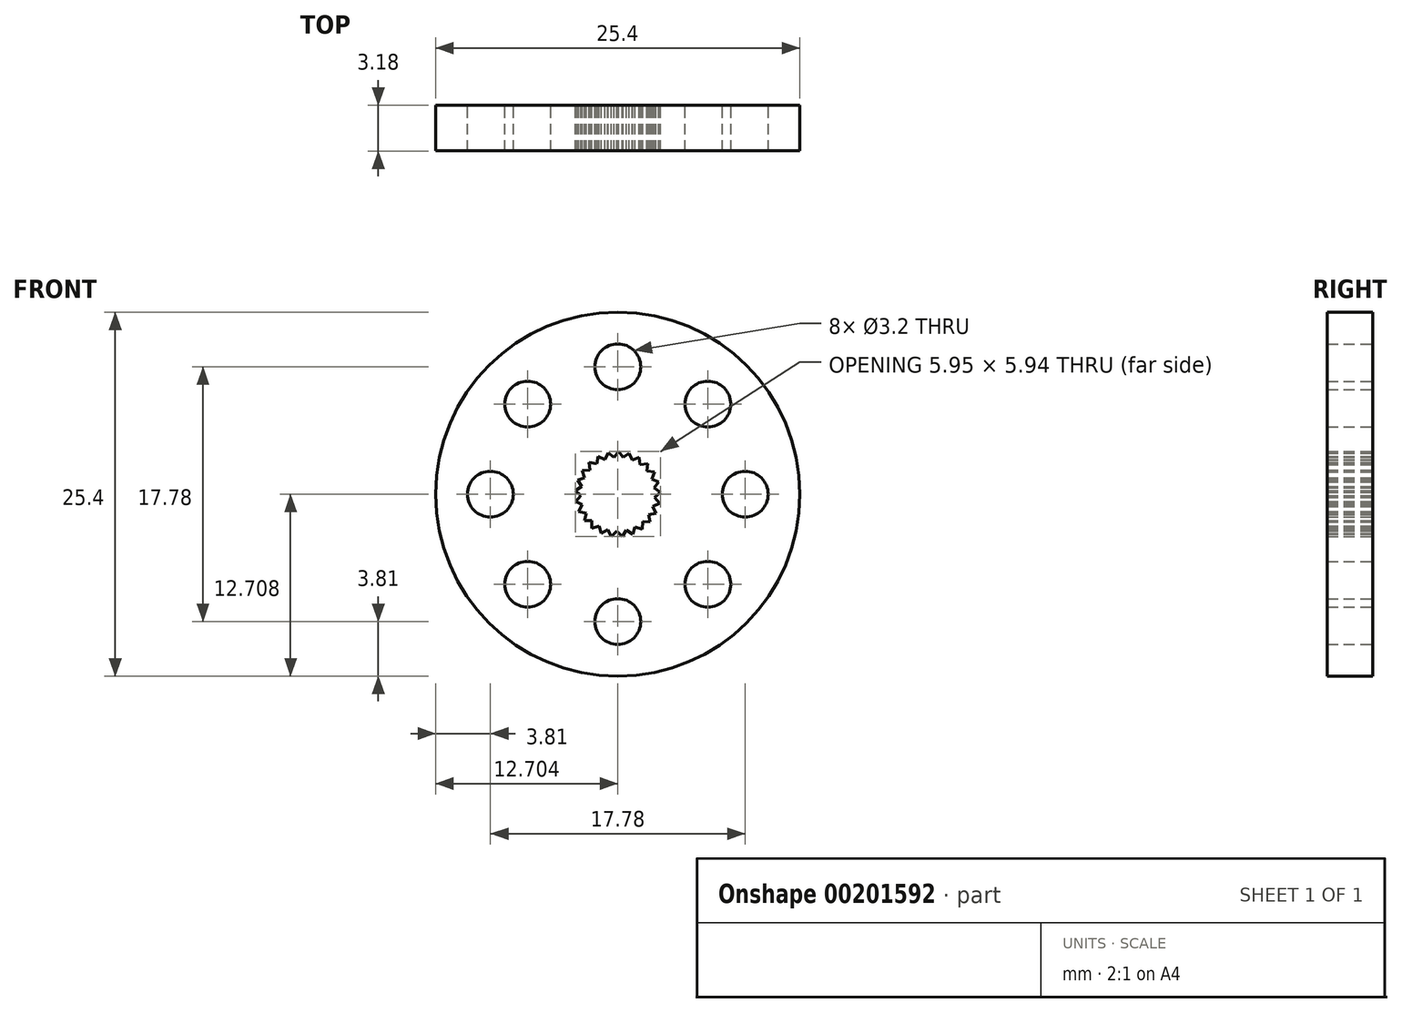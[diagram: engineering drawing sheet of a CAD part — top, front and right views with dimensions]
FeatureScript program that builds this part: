
annotation { "Feature Type Name" : "Feature", "Feature Type Description" : "" }
export const myFeature = defineFeature(function(context is Context, id is Id, definition is map)
    precondition{}
    {
        {
            var Q0;
            Q0=qCreatedBy(makeId("Front.planeOp"),FACE);
            var sketch = newSketch(context, id + "F0", { "sketchPlane" : qUnion([Q0])});
            skCircle(sketch, "E0", {"center": v(0, 0) * mm, "radius": 12.7 * mm});
            skCircle(sketch, "E1", {"center": v(0, 8.9) * mm, "radius": 1.6 * mm});
            skLineSegment(sketch, "E2", {"start": v(-2.48, 1.65) * mm, "end": v(-2.31, 1.15) * mm});
            skLineSegment(sketch, "E3", {"start": v(-2.31, 1.15) * mm, "end": v(-2.81, 0.98) * mm});
            skLineSegment(sketch, "E4.1.0", {"start": v(-2.81, 0.98) * mm, "end": v(-2.53, 0.54) * mm});
            skLineSegment(sketch, "E4.1.1", {"start": v(-2.53, 0.54) * mm, "end": v(-2.97, 0.25) * mm});
            skLineSegment(sketch, "E4.2.0", {"start": v(-2.97, 0.25) * mm, "end": v(-2.58, -0.1) * mm});
            skLineSegment(sketch, "E4.2.1", {"start": v(-2.58, -0.1) * mm, "end": v(-2.94, -0.5) * mm});
            skLineSegment(sketch, "E4.3.0", {"start": v(-2.94, -0.5) * mm, "end": v(-2.47, -0.74) * mm});
            skLineSegment(sketch, "E4.3.1", {"start": v(-2.47, -0.74) * mm, "end": v(-2.72, -1.2) * mm});
            skLineSegment(sketch, "E4.4.0", {"start": v(-2.72, -1.2) * mm, "end": v(-2.21, -1.34) * mm});
            skLineSegment(sketch, "E4.4.1", {"start": v(-2.21, -1.34) * mm, "end": v(-2.34, -1.85) * mm});
            skLineSegment(sketch, "E4.5.0", {"start": v(-2.34, -1.85) * mm, "end": v(-1.8, -1.84) * mm});
            skLineSegment(sketch, "E4.5.1", {"start": v(-1.8, -1.84) * mm, "end": v(-1.8, -2.37) * mm});
            skLineSegment(sketch, "E4.6.0", {"start": v(-1.8, -2.37) * mm, "end": v(-1.3, -2.24) * mm});
            skLineSegment(sketch, "E4.6.1", {"start": v(-1.3, -2.24) * mm, "end": v(-1.16, -2.75) * mm});
            skLineSegment(sketch, "E4.7.0", {"start": v(-1.16, -2.75) * mm, "end": v(-0.7, -2.49) * mm});
            skLineSegment(sketch, "E4.7.1", {"start": v(-0.7, -2.49) * mm, "end": v(-0.44, -2.95) * mm});
            skLineSegment(sketch, "E4.8.0", {"start": v(-0.44, -2.95) * mm, "end": v(-0.06, -2.58) * mm});
            skLineSegment(sketch, "E4.8.1", {"start": v(-0.06, -2.58) * mm, "end": v(0.3, -2.96) * mm});
            skLineSegment(sketch, "E4.9.0", {"start": v(0.3, -2.96) * mm, "end": v(0.59, -2.52) * mm});
            skLineSegment(sketch, "E4.9.1", {"start": v(0.59, -2.52) * mm, "end": v(1.04, -2.8) * mm});
            skLineSegment(sketch, "E4.10.0", {"start": v(1.04, -2.8) * mm, "end": v(1.2, -2.3) * mm});
            skLineSegment(sketch, "E4.10.1", {"start": v(1.2, -2.3) * mm, "end": v(1.7, -2.45) * mm});
            skLineSegment(sketch, "E4.11.0", {"start": v(1.7, -2.45) * mm, "end": v(1.73, -1.92) * mm});
            skLineSegment(sketch, "E4.11.1", {"start": v(1.73, -1.92) * mm, "end": v(2.25, -1.95) * mm});
            skLineSegment(sketch, "E4.12.0", {"start": v(2.25, -1.95) * mm, "end": v(2.15, -1.43) * mm});
            skLineSegment(sketch, "E4.12.1", {"start": v(2.15, -1.43) * mm, "end": v(2.67, -1.33) * mm});
            skLineSegment(sketch, "E4.13.0", {"start": v(2.67, -1.33) * mm, "end": v(2.44, -0.85) * mm});
            skLineSegment(sketch, "E4.13.1", {"start": v(2.44, -0.85) * mm, "end": v(2.91, -0.62) * mm});
            skLineSegment(sketch, "E4.14.0", {"start": v(2.91, -0.62) * mm, "end": v(2.57, -0.22) * mm});
            skLineSegment(sketch, "E4.14.1", {"start": v(2.57, -0.22) * mm, "end": v(2.98, 0.12) * mm});
            skLineSegment(sketch, "E4.15.0", {"start": v(2.98, 0.12) * mm, "end": v(2.55, 0.43) * mm});
            skLineSegment(sketch, "E4.15.1", {"start": v(2.55, 0.43) * mm, "end": v(2.85, 0.86) * mm});
            skLineSegment(sketch, "E4.16.0", {"start": v(2.85, 0.86) * mm, "end": v(2.36, 1.05) * mm});
            skLineSegment(sketch, "E4.16.1", {"start": v(2.36, 1.05) * mm, "end": v(2.55, 1.54) * mm});
            skLineSegment(sketch, "E4.17.0", {"start": v(2.55, 1.54) * mm, "end": v(2.03, 1.6) * mm});
            skLineSegment(sketch, "E4.17.1", {"start": v(2.03, 1.6) * mm, "end": v(2.09, 2.13) * mm});
            skLineSegment(sketch, "E4.18.0", {"start": v(2.09, 2.13) * mm, "end": v(1.56, 2.06) * mm});
            skLineSegment(sketch, "E4.18.1", {"start": v(1.56, 2.06) * mm, "end": v(1.5, 2.58) * mm});
            skLineSegment(sketch, "E4.19.0", {"start": v(1.5, 2.58) * mm, "end": v(1, 2.38) * mm});
            skLineSegment(sketch, "E4.19.1", {"start": v(1, 2.38) * mm, "end": v(0.8, 2.87) * mm});
            skLineSegment(sketch, "E4.20.0", {"start": v(0.8, 2.87) * mm, "end": v(0.38, 2.56) * mm});
            skLineSegment(sketch, "E4.20.1", {"start": v(0.38, 2.56) * mm, "end": v(0.07, 2.98) * mm});
            skLineSegment(sketch, "E4.21.0", {"start": v(0.07, 2.98) * mm, "end": v(-0.27, 2.57) * mm});
            skLineSegment(sketch, "E4.21.1", {"start": v(-0.27, 2.57) * mm, "end": v(-0.68, 2.9) * mm});
            skLineSegment(sketch, "E4.22.0", {"start": v(-0.68, 2.9) * mm, "end": v(-0.9, 2.42) * mm});
            skLineSegment(sketch, "E4.22.1", {"start": v(-0.9, 2.42) * mm, "end": v(-1.38, 2.64) * mm});
            skLineSegment(sketch, "E4.23.0", {"start": v(-1.38, 2.64) * mm, "end": v(-1.47, 2.12) * mm});
            skLineSegment(sketch, "E4.23.1", {"start": v(-1.47, 2.12) * mm, "end": v(-2, 2.22) * mm});
            skLineSegment(sketch, "E4.24.0", {"start": v(-2, 2.22) * mm, "end": v(-1.95, 1.69) * mm});
            skLineSegment(sketch, "E4.24.1", {"start": v(-1.95, 1.69) * mm, "end": v(-2.48, 1.65) * mm});
            skCircle(sketch, "E5.1.0", {"center": v(-6.29, 6.29) * mm, "radius": 1.6 * mm});
            skCircle(sketch, "E5.2.0", {"center": v(-8.9, 0) * mm, "radius": 1.6 * mm});
            skCircle(sketch, "E5.3.0", {"center": v(-6.29, -6.29) * mm, "radius": 1.6 * mm});
            skCircle(sketch, "E5.4.0", {"center": v(0, -8.9) * mm, "radius": 1.6 * mm});
            skCircle(sketch, "E5.5.0", {"center": v(6.29, -6.29) * mm, "radius": 1.6 * mm});
            skCircle(sketch, "E5.6.0", {"center": v(8.9, 0) * mm, "radius": 1.6 * mm});
            skCircle(sketch, "E5.7.0", {"center": v(6.29, 6.29) * mm, "radius": 1.6 * mm});
            skSolve(sketch);
        }
        {
            var Q0;
            Q0=makeQuery(id+"F0.imprint","IMPRINT",FACE,{"disambiguationData":[TD([[makeQuery(id+"F0.imprint","IMPRINT",EDGE,{"derivedFrom":sQuery(id+"F0.wireOp",EDGE,"E0")}),1.0]])]});
            extrude(context, id + "F1", {"entities" : qUnion([Q0]), "depth" : 3.17 * mm});
        }
    });
